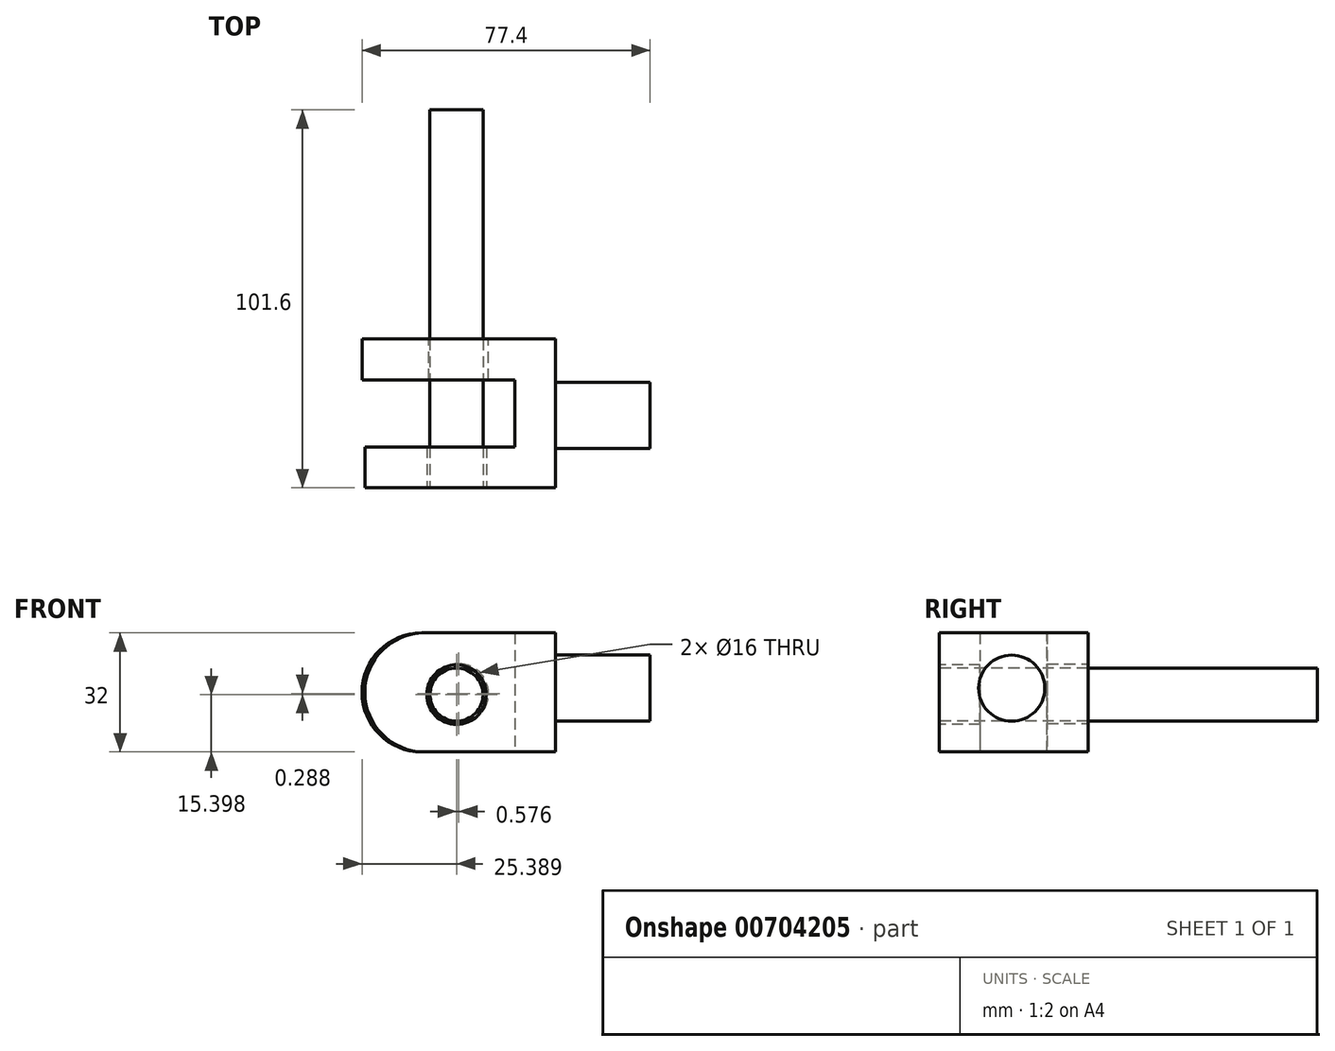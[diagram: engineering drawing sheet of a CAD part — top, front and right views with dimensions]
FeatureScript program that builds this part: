
annotation { "Feature Type Name" : "Feature", "Feature Type Description" : "" }
export const myFeature = defineFeature(function(context is Context, id is Id, definition is map)
    precondition{}
    {
        {
            var Q0;
            Q0=qCreatedBy(makeId("Top.planeOp"),FACE);
            var sketch = newSketch(context, id + "F0", { "sketchPlane" : qUnion([Q0])});
            skLineSegment(sketch, "E0", {"start": v(-36.47, 29) * mm, "end": v(-36.47, 18) * mm});
            skLineSegment(sketch, "E1", {"start": v(-36.47, 18) * mm, "end": v(4.53, 18) * mm});
            skLineSegment(sketch, "E2", {"start": v(4.53, 18) * mm, "end": v(4.53, 0) * mm});
            skLineSegment(sketch, "E3", {"start": v(4.53, 0) * mm, "end": v(-35.7, 0) * mm});
            skLineSegment(sketch, "E4", {"start": v(-35.7, 0) * mm, "end": v(-35.7, -11) * mm});
            skLineSegment(sketch, "E5", {"start": v(-35.7, -11) * mm, "end": v(15.53, -11) * mm});
            skLineSegment(sketch, "E6", {"start": v(15.53, -11) * mm, "end": v(15.53, 29) * mm});
            skLineSegment(sketch, "E7", {"start": v(15.53, 29) * mm, "end": v(-36.47, 29) * mm});
            skSolve(sketch);
        }
        {
            var Q0;
            Q0 = qSketchRegion(id + "F0", true);
            extrude(context, id + "F1", {"entities" : qUnion([Q0]), "depth" : 32 * mm, "offsetDistance" : 25.4 * mm});
        }
        {
            var Q0;
            Q0=makeQuery(id+"F1.opExtrude","SWEPT_FACE",FACE,{"disambiguationData":[OSD([sQuery(id+"F0.wireOp",EDGE,"E5")])]});
            var sketch = newSketch(context, id + "F2", { "sketchPlane" : qUnion([Q0])});
            skCircle(sketch, "E8", {"center": v(-11.08, 15.4) * mm, "radius": 8 * mm});
            skSolve(sketch);
        }
        {
            var Q0;
            Q0 = qSketchRegion(id + "F2", true);
            extrude(context, id + "F3", {"entities" : qUnion([Q0]), "operationType" : NewBodyOperationType.REMOVE, "oppositeDirection" : true, "depth" : 25.4 * mm, "offsetDistance" : 25.4 * mm});
        }
        {
            var Q0;
            Q0=makeQuery(id+"F1.opExtrude","SWEPT_FACE",FACE,{"disambiguationData":[OSD([sQuery(id+"F0.wireOp",EDGE,"E7")])]});
            var sketch = newSketch(context, id + "F4", { "sketchPlane" : qUnion([Q0])});
            skCircle(sketch, "E9", {"center": v(10.5, 15.69) * mm, "radius": 8 * mm});
            skSolve(sketch);
        }
        {
            var Q0;
            Q0 = qSketchRegion(id + "F4", true);
            extrude(context, id + "F5", {"entities" : qUnion([Q0]), "operationType" : NewBodyOperationType.REMOVE, "oppositeDirection" : true, "depth" : 25.4 * mm, "offsetDistance" : 25.4 * mm});
        }
        {
            var Q0;
            Q0=makeQuery(id+"F1.opExtrude","CAP_EDGE",EDGE,{"disambiguationData":[OSD([sQuery(id+"F0.wireOp",EDGE,"E4")])],"isStart":false});
            fillet(context, id + "F6", {"entities" : qUnion([Q0]), "radius" : 16 * mm, "tangentPropagation" : true, "allowEdgeOverflow" : false});
        }
        {
            var Q0;
            Q0=makeQuery(id+"F1.opExtrude","CAP_EDGE",EDGE,{"disambiguationData":[OSD([sQuery(id+"F0.wireOp",EDGE,"E4")])],"isStart":true});
            fillet(context, id + "F7", {"entities" : qUnion([Q0]), "radius" : 16 * mm, "tangentPropagation" : true, "allowEdgeOverflow" : false});
        }
        {
            var Q0;
            Q0=makeQuery(id+"F1.opExtrude","CAP_EDGE",EDGE,{"disambiguationData":[OSD([sQuery(id+"F0.wireOp",EDGE,"E0")])],"isStart":false});
            fillet(context, id + "F8", {"entities" : qUnion([Q0]), "radius" : 16 * mm, "tangentPropagation" : true, "allowEdgeOverflow" : false});
        }
        {
            var Q0;
            Q0=makeQuery(id+"F1.opExtrude","CAP_EDGE",EDGE,{"disambiguationData":[OSD([sQuery(id+"F0.wireOp",EDGE,"E0")])],"isStart":true});
            fillet(context, id + "F9", {"entities" : qUnion([Q0]), "radius" : 16 * mm, "tangentPropagation" : true, "allowEdgeOverflow" : false});
        }
        {
            var Q0;
            Q0=makeQuery(id+"F1.opExtrude","SWEPT_FACE",FACE,{"disambiguationData":[OSD([sQuery(id+"F0.wireOp",EDGE,"E6")])]});
            var sketch = newSketch(context, id + "F10", { "sketchPlane" : qUnion([Q0])});
            skCircle(sketch, "E10", {"center": v(8.5, 17.12) * mm, "radius": 8.89 * mm});
            skSolve(sketch);
        }
        {
            var Q0;
            Q0 = qSketchRegion(id + "F10", true);
            extrude(context, id + "F11", {"entities" : qUnion([Q0]), "operationType" : NewBodyOperationType.ADD, "depth" : 25.4 * mm, "offsetDistance" : 25.4 * mm});
        }
        {
            var Q0;
            Q0=makeQuery(id+"F1.opExtrude","SWEPT_FACE",FACE,{"disambiguationData":[OSD([sQuery(id+"F0.wireOp",EDGE,"E5")])]});
            var sketch = newSketch(context, id + "F12", { "sketchPlane" : qUnion([Q0])});
            skCircle(sketch, "E11", {"center": v(-11.08, 15.4) * mm, "radius": 7.13 * mm});
            skSolve(sketch);
        }
        {
            var Q0;
            Q0 = qSketchRegion(id + "F12", true);
            extrude(context, id + "F13", {"entities" : qUnion([Q0]), "oppositeDirection" : true, "depth" : 101.6 * mm, "offsetDistance" : 25.4 * mm});
        }
    });
